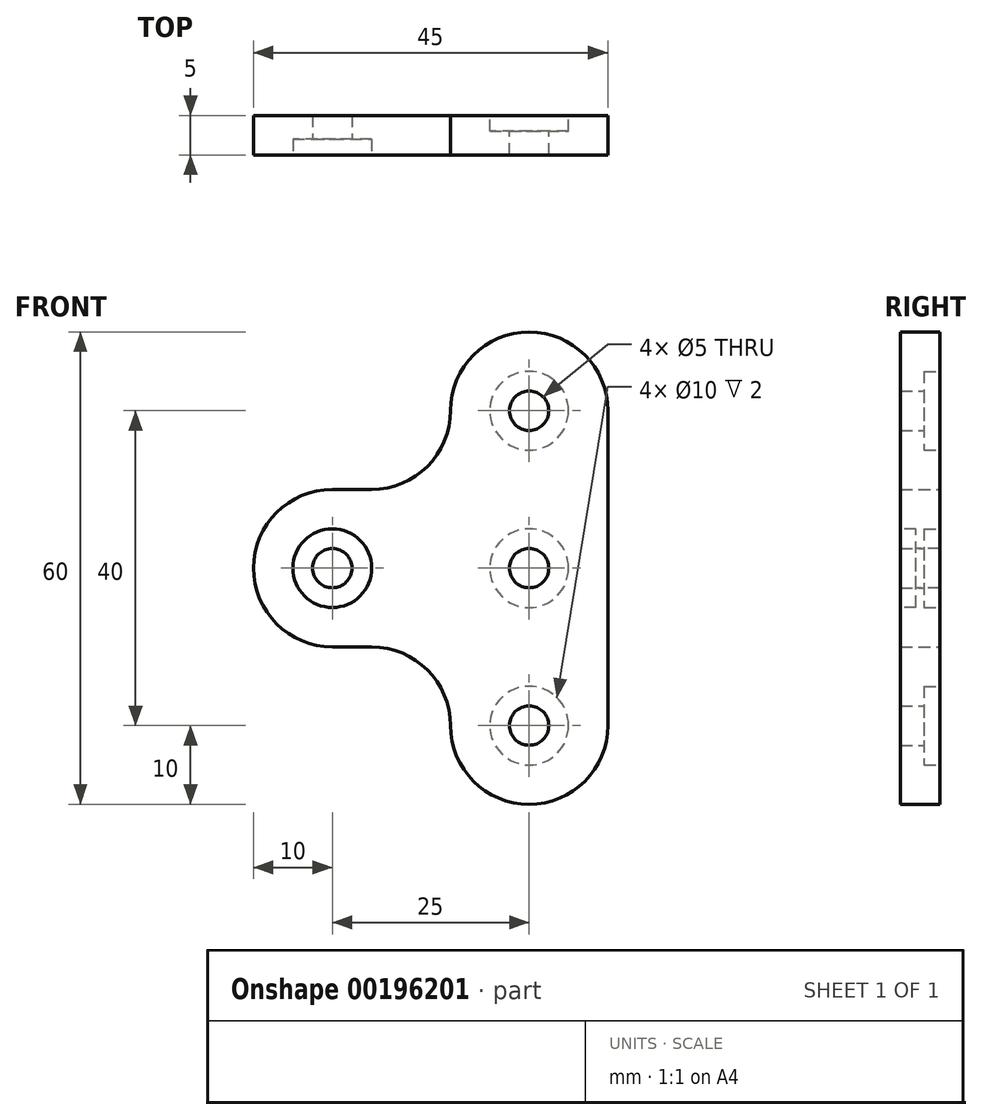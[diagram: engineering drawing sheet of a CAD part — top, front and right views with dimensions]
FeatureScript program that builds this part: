
annotation { "Feature Type Name" : "Feature", "Feature Type Description" : "" }
export const myFeature = defineFeature(function(context is Context, id is Id, definition is map)
    precondition{}
    {
        {
            var Q0;
            Q0=qCreatedBy(makeId("Front.planeOp"),FACE);
            var sketch = newSketch(context, id + "F0", { "sketchPlane" : qUnion([Q0])});
            skPoint(sketch, "E0", {"position": v(25, 20) * mm});
            skPoint(sketch, "E1", {"position": v(25, -20) * mm});
            skLineSegment(sketch, "E2", {"start": v(0, 0) * mm, "end": v(114.75, 0) * mm, "construction": true});
            skLineSegment(sketch, "E3", {"start": v(0, 0) * mm, "end": v(0, 57.65) * mm, "construction": true});
            skLineSegment(sketch, "E4.bottom", {"start": v(-10, 10) * mm, "end": v(15, 10) * mm});
            skLineSegment(sketch, "E4.top", {"start": v(-10, -10) * mm, "end": v(15, -10) * mm});
            skLineSegment(sketch, "E4.left", {"start": v(-10, 10) * mm, "end": v(-10, -10) * mm});
            skLineSegment(sketch, "E5.bottom", {"start": v(35, 30) * mm, "end": v(15, 30) * mm});
            skLineSegment(sketch, "E5.top", {"start": v(35, -30) * mm, "end": v(15, -30) * mm});
            skLineSegment(sketch, "E5.left", {"start": v(35, 30) * mm, "end": v(35, 10) * mm});
            skLineSegment(sketch, "E5.right", {"start": v(15, 30) * mm, "end": v(15, 10) * mm});
            skPoint(sketch, "E6", {"position": v(25, 30) * mm});
            skPoint(sketch, "E7", {"position": v(25, -30) * mm});
            skPoint(sketch, "E8", {"position": v(35, 0) * mm});
            skPoint(sketch, "E9", {"position": v(-10, 0) * mm});
            skLineSegment(sketch, "E10.trimOffspring", {"start": v(15, -10) * mm, "end": v(15, -30) * mm});
            skPoint(sketch, "E11", {"position": v(25, 0) * mm});
            skLineSegment(sketch, "E12.bottom", {"start": v(35, 10) * mm, "end": v(35, 10) * mm});
            skLineSegment(sketch, "E12.top", {"start": v(35, -10) * mm, "end": v(35, -10) * mm});
            skLineSegment(sketch, "E12.right", {"start": v(35, 10) * mm, "end": v(35, -10) * mm});
            skLineSegment(sketch, "E13.trimOffspring", {"start": v(35, -10) * mm, "end": v(35, -30) * mm});
            skPoint(sketch, "E4.right.end.orphan", {"position": v(35, -10) * mm});
            skSolve(sketch);
        }
        {
            var Q0;
            Q0=makeQuery(id+"F0.imprint","IMPRINT",FACE,{"disambiguationData":[TD([[makeQuery(id+"F0.imprint","IMPRINT",EDGE,{"derivedFrom":sQuery(id+"F0.wireOp",EDGE,"E4.bottom")}),-1.0]])]});
            extrude(context, id + "F1", {"entities" : qUnion([Q0]), "depth" : 5 * mm});
        }
        {
            var Q0;
            Q0=sQuery(id+"F0.wireOp",VERTEX,"E0");
            var Q1;
            Q1=sQuery(id+"F0.wireOp",VERTEX,"E1");
            var Q2;
            Q2=sQuery(id+"F0.wireOp",VERTEX,"E11");
            var Q3;
            Q3=makeQuery(id+"F1.opExtrude","SWEPT_BODY",BODY,{"disambiguationData":[OSD([sQuery(id+"F0.wireOp",EDGE,"E4.bottom"),sQuery(id+"F0.wireOp",EDGE,"E4.top"),sQuery(id+"F0.wireOp",EDGE,"E4.left"),sQuery(id+"F0.wireOp",EDGE,"E5.bottom"),sQuery(id+"F0.wireOp",EDGE,"E5.top"),sQuery(id+"F0.wireOp",EDGE,"E5.left"),sQuery(id+"F0.wireOp",EDGE,"E5.right"),sQuery(id+"F0.wireOp",EDGE,"E10.trimOffspring")])]});
            hole(context, id + "F2", {"style" : HoleStyle.C_BORE, "endStyle" : HoleEndStyle.THROUGH, "oppositeDirection" : true, "holeDiameter" : 5 * mm, "cBoreDiameter" : 10 * mm, "cBoreDepth" : 2 * mm, "locations" : qUnion([Q0, Q1, Q2]), "scope" : qUnion([Q3]), "isTappedThrough" : true});
        }
        {
            var Q0;
            Q0=makeQuery(id+"F1.opExtrude","SWEPT_EDGE",EDGE,{"disambiguationData":[OSD([sQuery(id+"F0.wireOp",EDGE,"E5.bottom"),sQuery(id+"F0.wireOp",EDGE,"E5.left")])]});
            var Q1;
            Q1=makeQuery(id+"F1.opExtrude","SWEPT_EDGE",EDGE,{"disambiguationData":[OSD([sQuery(id+"F0.wireOp",EDGE,"E5.top"),sQuery(id+"F0.wireOp",EDGE,"E13.trimOffspring")])]});
            var Q2;
            Q2=makeQuery(id+"F1.opExtrude","SWEPT_EDGE",EDGE,{"disambiguationData":[OSD([sQuery(id+"F0.wireOp",EDGE,"E5.top"),sQuery(id+"F0.wireOp",EDGE,"E10.trimOffspring")])]});
            var Q3;
            Q3=makeQuery(id+"F1.opExtrude","SWEPT_EDGE",EDGE,{"disambiguationData":[OSD([sQuery(id+"F0.wireOp",EDGE,"E5.bottom"),sQuery(id+"F0.wireOp",EDGE,"E5.right")])]});
            var Q4;
            Q4=makeQuery(id+"F1.opExtrude","SWEPT_EDGE",EDGE,{"disambiguationData":[OSD([sQuery(id+"F0.wireOp",EDGE,"E5.bottom"),sQuery(id+"F0.wireOp",EDGE,"E5.left")])]});
            var Q5;
            Q5=makeQuery(id+"F1.opExtrude","SWEPT_EDGE",EDGE,{"disambiguationData":[OSD([sQuery(id+"F0.wireOp",EDGE,"E4.bottom"),sQuery(id+"F0.wireOp",EDGE,"E4.left")])]});
            var Q6;
            Q6=makeQuery(id+"F1.opExtrude","SWEPT_EDGE",EDGE,{"disambiguationData":[OSD([sQuery(id+"F0.wireOp",EDGE,"E4.top"),sQuery(id+"F0.wireOp",EDGE,"E4.left")])]});
            var Q7;
            Q7=makeQuery(id+"F1.opExtrude","SWEPT_EDGE",EDGE,{"disambiguationData":[OSD([sQuery(id+"F0.wireOp",EDGE,"E5.top"),sQuery(id+"F0.wireOp",EDGE,"E10.trimOffspring")])]});
            var Q8;
            Q8=makeQuery(id+"F1.opExtrude","SWEPT_EDGE",EDGE,{"disambiguationData":[OSD([sQuery(id+"F0.wireOp",EDGE,"E12.bottom"),sQuery(id+"F0.wireOp",EDGE,"E12.right")])]});
            var Q9;
            Q9=makeQuery(id+"F1.opExtrude","SWEPT_EDGE",EDGE,{"disambiguationData":[OSD([sQuery(id+"F0.wireOp",EDGE,"E12.top"),sQuery(id+"F0.wireOp",EDGE,"E12.right")])]});
            var Q10;
            Q10=makeQuery(id+"F1.opExtrude","SWEPT_EDGE",EDGE,{"disambiguationData":[OSD([sQuery(id+"F0.wireOp",EDGE,"E4.bottom"),sQuery(id+"F0.wireOp",EDGE,"E5.right")])]});
            var Q11;
            Q11=makeQuery(id+"F1.opExtrude","SWEPT_EDGE",EDGE,{"disambiguationData":[OSD([sQuery(id+"F0.wireOp",EDGE,"E4.top"),sQuery(id+"F0.wireOp",EDGE,"E10.trimOffspring")])]});
            fillet(context, id + "F3", {"entities" : qUnion([Q0, Q1, Q2, Q3, Q4, Q5, Q6, Q7, Q8, Q9, Q10, Q11]), "radius" : 10 * mm, "tangentPropagation" : true, "allowEdgeOverflow" : false});
        }
        {
            var Q0;
            Q0=makeQuery(id+"F1.opExtrude","CAP_FACE",FACE,{"disambiguationData":[OSD([sQuery(id+"F0.wireOp",EDGE,"E4.bottom"),sQuery(id+"F0.wireOp",EDGE,"E4.top"),sQuery(id+"F0.wireOp",EDGE,"E4.left"),sQuery(id+"F0.wireOp",EDGE,"E5.bottom"),sQuery(id+"F0.wireOp",EDGE,"E5.top"),sQuery(id+"F0.wireOp",EDGE,"E5.left"),sQuery(id+"F0.wireOp",EDGE,"E5.right"),sQuery(id+"F0.wireOp",EDGE,"E10.trimOffspring"),sQuery(id+"F0.wireOp",EDGE,"E12.bottom"),sQuery(id+"F0.wireOp",EDGE,"E12.top"),sQuery(id+"F0.wireOp",EDGE,"E12.right"),sQuery(id+"F0.wireOp",EDGE,"E13.trimOffspring")])],"isStart":false});
            var sketch = newSketch(context, id + "F4", { "sketchPlane" : qUnion([Q0])});
            skPoint(sketch, "E14", {"position": v(0, 0) * mm});
            skSolve(sketch);
        }
        {
            var Q0;
            Q0=sQuery(id+"F4.wireOp",VERTEX,"E14");
            var Q1;
            Q1=makeQuery(id+"F1.opExtrude","SWEPT_BODY",BODY,{"disambiguationData":[OSD([sQuery(id+"F0.wireOp",EDGE,"E4.bottom"),sQuery(id+"F0.wireOp",EDGE,"E4.top"),sQuery(id+"F0.wireOp",EDGE,"E4.left"),sQuery(id+"F0.wireOp",EDGE,"E5.bottom"),sQuery(id+"F0.wireOp",EDGE,"E5.top"),sQuery(id+"F0.wireOp",EDGE,"E5.left"),sQuery(id+"F0.wireOp",EDGE,"E5.right"),sQuery(id+"F0.wireOp",EDGE,"E10.trimOffspring"),sQuery(id+"F0.wireOp",EDGE,"E12.bottom"),sQuery(id+"F0.wireOp",EDGE,"E12.top"),sQuery(id+"F0.wireOp",EDGE,"E12.right"),sQuery(id+"F0.wireOp",EDGE,"E13.trimOffspring")])]});
            hole(context, id + "F5", {"style" : HoleStyle.C_BORE, "endStyle" : HoleEndStyle.THROUGH, "holeDiameter" : 5 * mm, "cBoreDiameter" : 10 * mm, "cBoreDepth" : 2 * mm, "locations" : qUnion([Q0]), "scope" : qUnion([Q1]), "isTappedThrough" : true});
        }
    });
